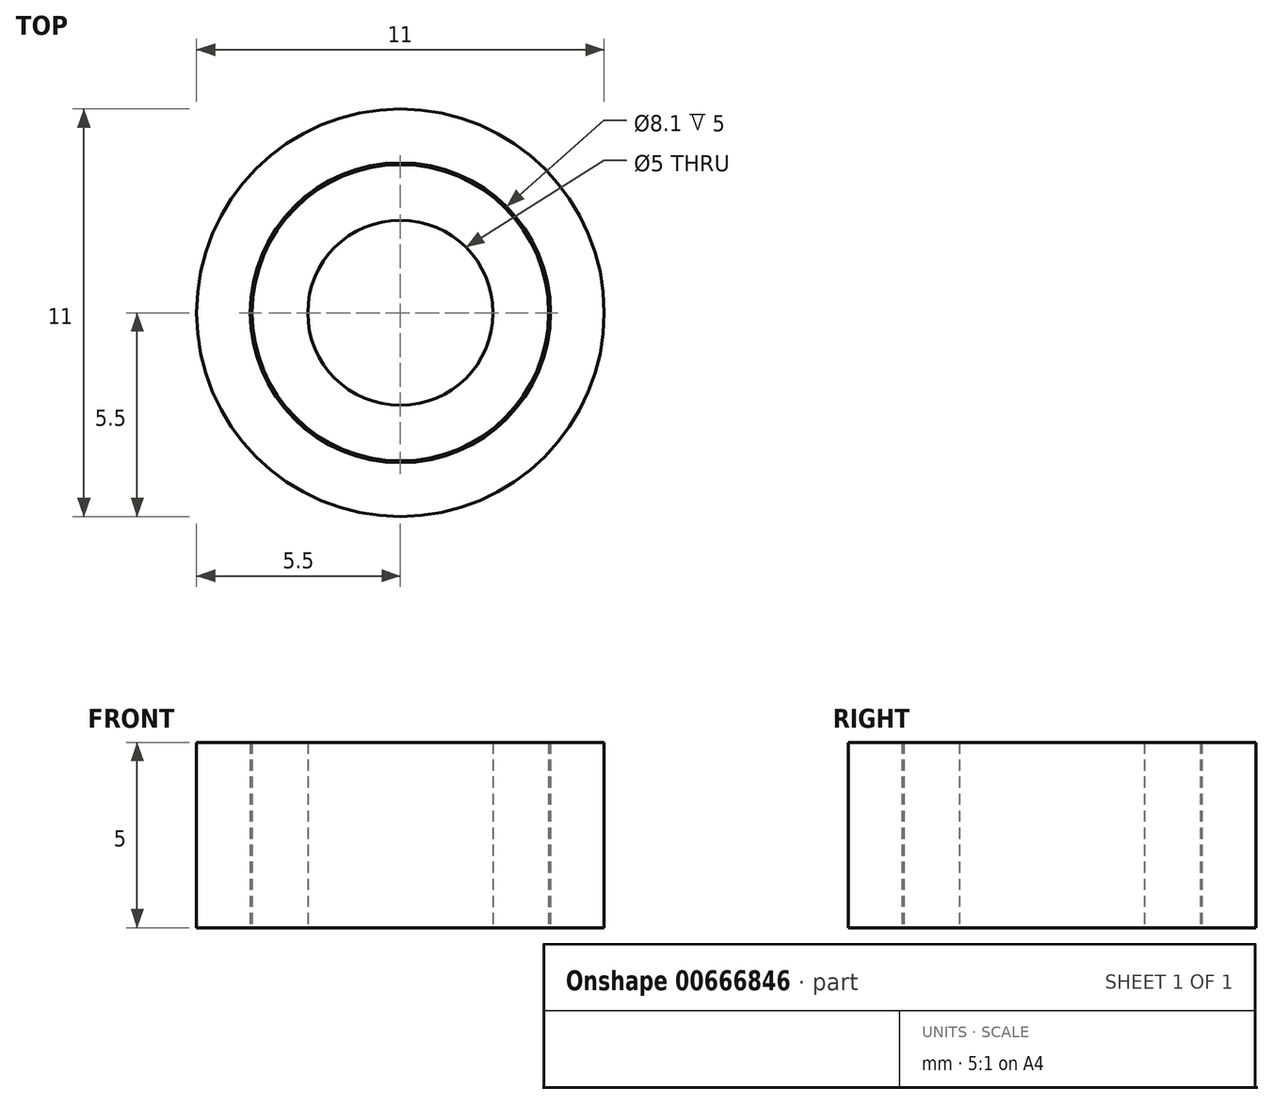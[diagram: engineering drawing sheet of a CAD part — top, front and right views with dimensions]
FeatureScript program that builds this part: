
annotation { "Feature Type Name" : "Feature", "Feature Type Description" : "" }
export const myFeature = defineFeature(function(context is Context, id is Id, definition is map)
    precondition{}
    {
        {
            var Q0;
            Q0=qCreatedBy(makeId("Top.planeOp"),FACE);
            var sketch = newSketch(context, id + "F0", { "sketchPlane" : qUnion([Q0])});
            skCircle(sketch, "E0", {"center": v(0, 0) * mm, "radius": 2.5 * mm});
            skCircle(sketch, "E1", {"center": v(0, 0) * mm, "radius": 4 * mm});
            skSolve(sketch);
        }
        {
            var Q0;
            Q0=qSketchRegion(id+"F0",true);
            extrude(context, id + "F1", {"entities" : qUnion([Q0]), "depth" : 5 * mm, "offsetDistance" : 25 * mm});
        }
        {
            var Q0;
            Q0=qCreatedBy(makeId("Top.planeOp"),FACE);
            var sketch = newSketch(context, id + "F2", { "sketchPlane" : qUnion([Q0])});
            skCircle(sketch, "E2", {"center": v(0, 0) * mm, "radius": 4.05 * mm});
            skCircle(sketch, "E3", {"center": v(0, 0) * mm, "radius": 5.5 * mm});
            skSolve(sketch);
        }
        {
            var Q0;
            Q0=qSketchRegion(id+"F2",true);
            extrude(context, id + "F3", {"entities" : qUnion([Q0]), "depth" : 5 * mm, "offsetDistance" : 25 * mm});
        }
    });
